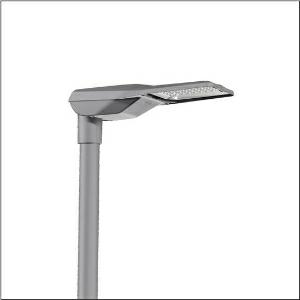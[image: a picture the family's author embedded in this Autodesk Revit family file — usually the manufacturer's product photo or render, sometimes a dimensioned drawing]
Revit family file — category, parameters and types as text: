
# Revit family: streetlight_sl_21_iq_mini___st0_8a_5xe2c41d08hb_7f29
name_source: partatom
category: Lighting Fixtures
units: mm (PartAtom-declared; Revit-internal decimal feet)

## family parameters
Cut with Voids When Loaded = No
Host = Face
Light Source = No
Part Type = Normal
Room Calculation Point = No
Round Connector Dimension = Use Diameter
Shared = No

## types (1)
- --- (1 x LED, 9860 lm, 70.9 W, 4000K)
    Apparent Load = 71 VA
    CIE Flux Codes = 38 75 97 100 100
    Color Rendering = 70
    Color Temperature = 4000K
    Default Elevation = 1800 mm
    Description = Streetlight SL 21 iQ mini, mast luminaire, primary light control with lens, of PMMA, primary optical cover: cover, of toughened safety glass, transparent, light distribution: ST0.8a, light emission: direct distribution, primary light characteristic: asymmetric, installation type: post-top, side-entry, LED, High Power LED, rated luminous flux: 9.860lm, luminous efficacy: 139lm/W, light colour: 740, colour temperature: 4000K, control gear: iQ-Comfort, control: Auto-Match, Temp-Guard, Lumen-Switch, Night-Set, Smart-Wire, Light-Fading, Desk-Remote (wireless, voltage-free reading and setting of iQ features in the workshop via application-optimized NFC function/RFID function), optimised constant luminous flux control (CLO 2.0), pre-setting: linear dimming characteristic, mains connection: 220..240V, AC, 50/60Hz, start of lifetime: 71W, end of service life: 75W, reduction: 31W, luminaire housing, of diecast aluminium, powder-coated, Siteco® metallic grey (DB 702S), corrosivity category C5 mid according to DIN EN ISO 12944, please order mast flange separately, inclination adjustable: 0°, 5°, 10°, 15°, sealing non-destructively replaceable, multi-level sealing system, length: 628mm, width: 235mm, height: 110mm, mast flange for spigot size: 42mm (side-entry): 5XC10008XM4, 60/48mm (side-entry/post-top): 5XC10108XM2, 76/60mm (side-entry/post-top): 5XC10108XM1, mounting height: 4..8m, protection rating (complete): IP66, insulation class (complete): insulation class II (safety insulation), certification: CE, ENEC, ENEC+, VDE, impact resistance: IK10, permissible operating ambient temperature for outdoor applications: -40..+50°C, standard-compliant lighting for roads and squares, packaging unit: 1 piece

Light Distribution: ST0.8a
    Height = 110 mm
    Lamp = 1 x LED
    Lamp Light Flux = 9860 lm
    Lamp Power = 70.9 W
    Lamp count = 1
    Length = 625 mm
    Luminous efficacy = 139 lm/W
    Manufacturer = Siteco
    ModVariant = No
    Model = 5XE2C41D08HB
    Number of Poles = 1
    OnlyDefault = Yes
    Power Factor = 1
    Product Name = Streetlight SL 21 iQ mini | ST0.8a
    Product group = mast luminaire | pylon top
    ProductGroupID = 6100
    Protection Class = Protection class II
    Protection Degree = IP 66
    RLX_Detail_Level = 1
    RLX_Emergency_Light_Flux = 0 lm
    RLX_Emergency_Type = 0
    RLX_Emergency_Type_DB = No
    RlxData = <blob elided: 26321 chars, md5=291ea504>
    Socket = socket
    Standby Power = 0 W
    System Light Flux = 9860 lm
    System Power = 71 W
    Type Comments = factory setting: luminous flux: 100 % | dim-lin: 254 | 711 mA
    Type Image = l_1003519.jpg
    URL = http://relux.com
    VarID = @adj_178831
    Voltage = 0 V
    Weight = 0.00 kg
    Width = 234 mm

## geometry (parser evidence)
native form markers: Blend x4, Sweep x11
no freeform markers — native parametric forms only
